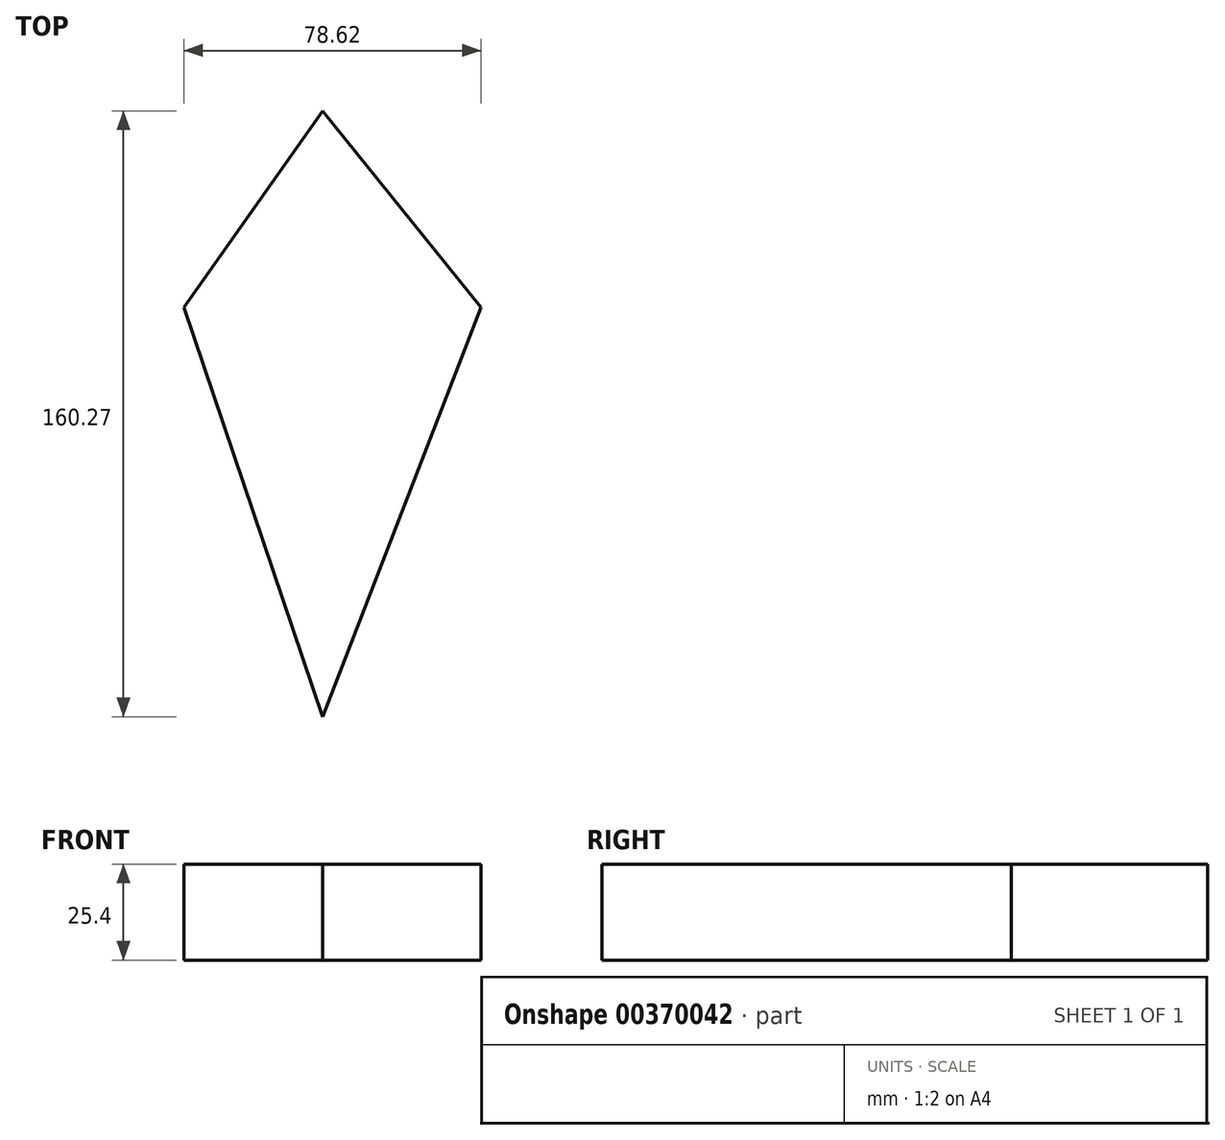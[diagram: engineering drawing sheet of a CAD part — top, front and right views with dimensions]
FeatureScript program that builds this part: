
annotation { "Feature Type Name" : "Feature", "Feature Type Description" : "" }
export const myFeature = defineFeature(function(context is Context, id is Id, definition is map)
    precondition{}
    {
        {
            var Q0;
            Q0=qCreatedBy(makeId("Top.planeOp"),FACE);
            var sketch = newSketch(context, id + "F0", { "sketchPlane" : qUnion([Q0])});
            skLineSegment(sketch, "E0", {"start": v(0, 51.94) * mm, "end": v(-36.7, 0) * mm});
            skLineSegment(sketch, "E1", {"start": v(-36.7, 0) * mm, "end": v(0, -108.33) * mm});
            skLineSegment(sketch, "E2", {"start": v(0, -108.33) * mm, "end": v(41.9, 0) * mm});
            skLineSegment(sketch, "E3", {"start": v(41.9, 0) * mm, "end": v(0, 51.94) * mm});
            skSolve(sketch);
        }
        {
            var Q0;
            Q0=makeQuery(id+"F0.imprint","IMPRINT",FACE,{"disambiguationData":[TD([[makeQuery(id+"F0.imprint","IMPRINT",EDGE,{"derivedFrom":sQuery(id+"F0.wireOp",EDGE,"E0")}),1.0]])]});
            extrude(context, id + "F1", {"entities" : qUnion([Q0]), "depth" : 25.4 * mm});
        }
    });
